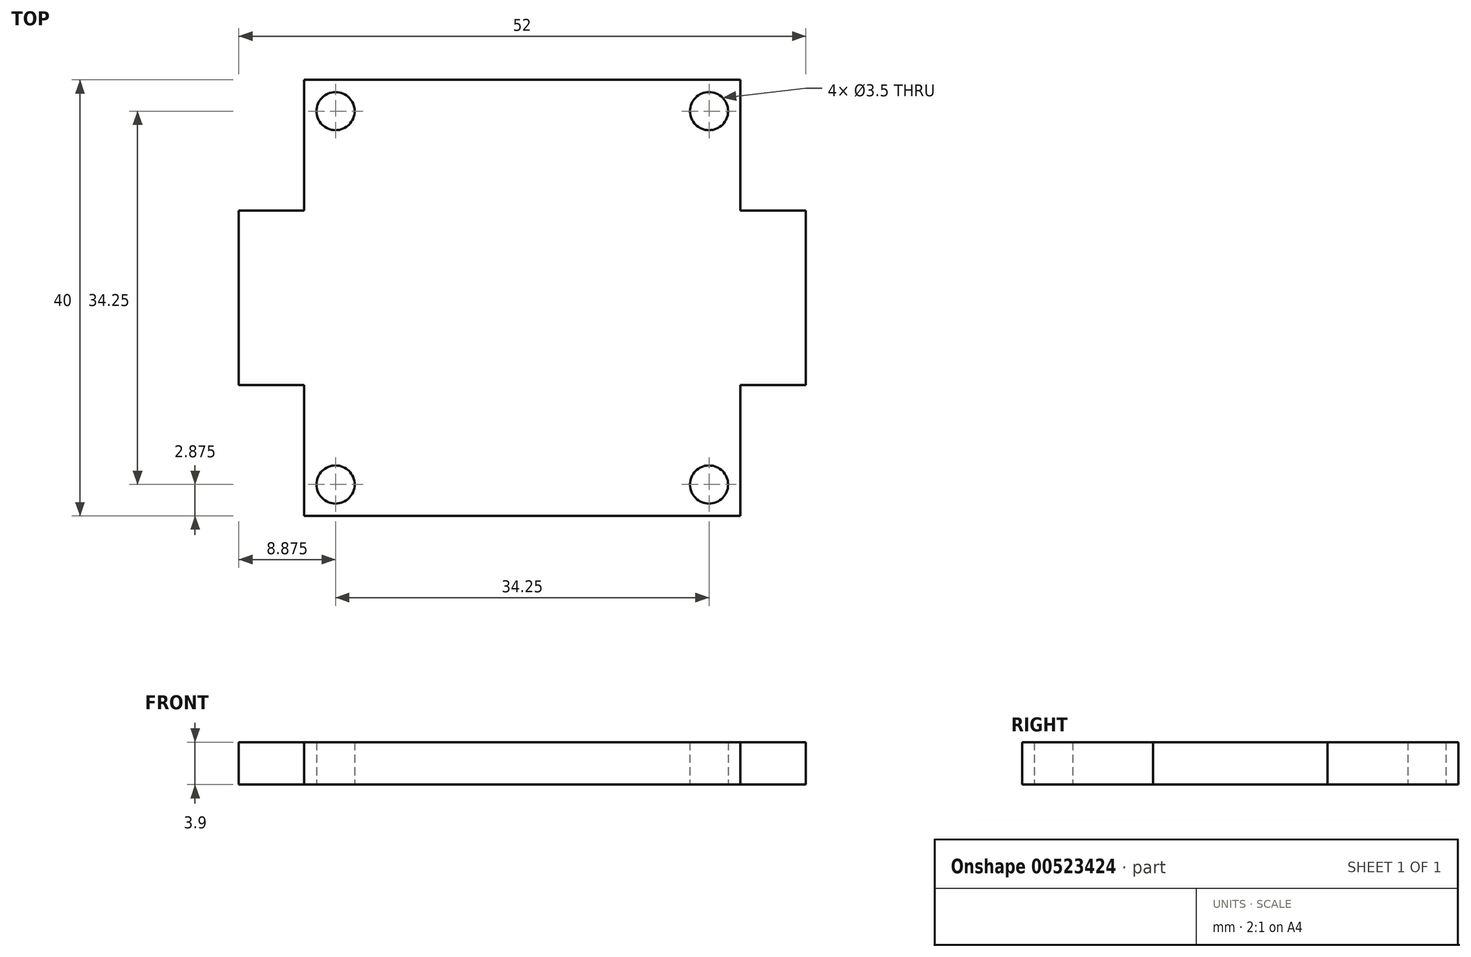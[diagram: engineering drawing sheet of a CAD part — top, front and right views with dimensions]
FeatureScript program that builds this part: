
annotation { "Feature Type Name" : "Feature", "Feature Type Description" : "" }
export const myFeature = defineFeature(function(context is Context, id is Id, definition is map)
    precondition{}
    {
        {
            var Q0;
            Q0=qCreatedBy(makeId("Top.planeOp"),FACE);
            var sketch = newSketch(context, id + "F0", { "sketchPlane" : qUnion([Q0])});
            skLineSegment(sketch, "E0.bottom", {"start": v(20, 20) * mm, "end": v(-20, 20) * mm});
            skLineSegment(sketch, "E0.top", {"start": v(20, -20) * mm, "end": v(-20, -20) * mm});
            skLineSegment(sketch, "E0.left", {"start": v(20, 20) * mm, "end": v(20, 8) * mm});
            skPoint(sketch, "E0.middle", {"position": v(0, 0) * mm});
            skLineSegment(sketch, "E1.bottom", {"start": v(-20, 8) * mm, "end": v(-26, 8) * mm});
            skLineSegment(sketch, "E1.top", {"start": v(-20, -8) * mm, "end": v(-26, -8) * mm});
            skLineSegment(sketch, "E1.right", {"start": v(-26, 8) * mm, "end": v(-26, -8) * mm});
            skLineSegment(sketch, "E2.bottom", {"start": v(20, 8) * mm, "end": v(26, 8) * mm});
            skLineSegment(sketch, "E2.top", {"start": v(20, -8) * mm, "end": v(26, -8) * mm});
            skLineSegment(sketch, "E2.right", {"start": v(26, 8) * mm, "end": v(26, -8) * mm});
            skLineSegment(sketch, "E3", {"start": v(-20, 0) * mm, "end": v(20, 0) * mm, "construction": true});
            skCircle(sketch, "E4", {"center": v(-17.12, 17.13) * mm, "radius": 1.75 * mm});
            skCircle(sketch, "E5", {"center": v(17.12, 17.13) * mm, "radius": 1.75 * mm});
            skCircle(sketch, "E6", {"center": v(17.12, -17.13) * mm, "radius": 1.75 * mm});
            skCircle(sketch, "E7", {"center": v(-17.12, -17.13) * mm, "radius": 1.75 * mm});
            skLineSegment(sketch, "E8.bottom", {"start": v(-17.12, 17.13) * mm, "end": v(17.12, 17.13) * mm, "construction": true});
            skLineSegment(sketch, "E8.top", {"start": v(-17.12, -17.13) * mm, "end": v(17.12, -17.13) * mm, "construction": true});
            skLineSegment(sketch, "E8.left", {"start": v(-17.12, 17.13) * mm, "end": v(-17.12, -17.13) * mm, "construction": true});
            skLineSegment(sketch, "E8.right", {"start": v(17.12, 17.13) * mm, "end": v(17.12, -17.13) * mm, "construction": true});
            skLineSegment(sketch, "E9", {"start": v(0, 17.13) * mm, "end": v(0, 20) * mm, "construction": true});
            skLineSegment(sketch, "E10", {"start": v(-17.12, 0) * mm, "end": v(-20, 0) * mm, "construction": true});
            skLineSegment(sketch, "E11.trimOffspring", {"start": v(-20, -8) * mm, "end": v(-20, -20) * mm});
            skLineSegment(sketch, "E12.trimOffspring", {"start": v(20, -8) * mm, "end": v(20, -20) * mm});
            skLineSegment(sketch, "E13", {"start": v(-20, 20) * mm, "end": v(-20, 8) * mm});
            skLineSegment(sketch, "E14", {"start": v(0, 20) * mm, "end": v(0, -20) * mm, "construction": true});
            skSolve(sketch);
        }
        {
            var Q0;
            Q0 = qSketchRegion(id + "F0", true);
            var Q1;
            Q1 = qConstructionFilter(qBodyType(qCreatedBy(id + "F0" ,EDGE), BodyType.WIRE), ConstructionObject.NO);
            extrude(context, id + "F1", {"entities" : qUnion([Q0]), "surfaceEntities" : qUnion([Q1]), "depth" : 3.9 * mm, "offsetDistance" : 25 * mm});
        }
    });
